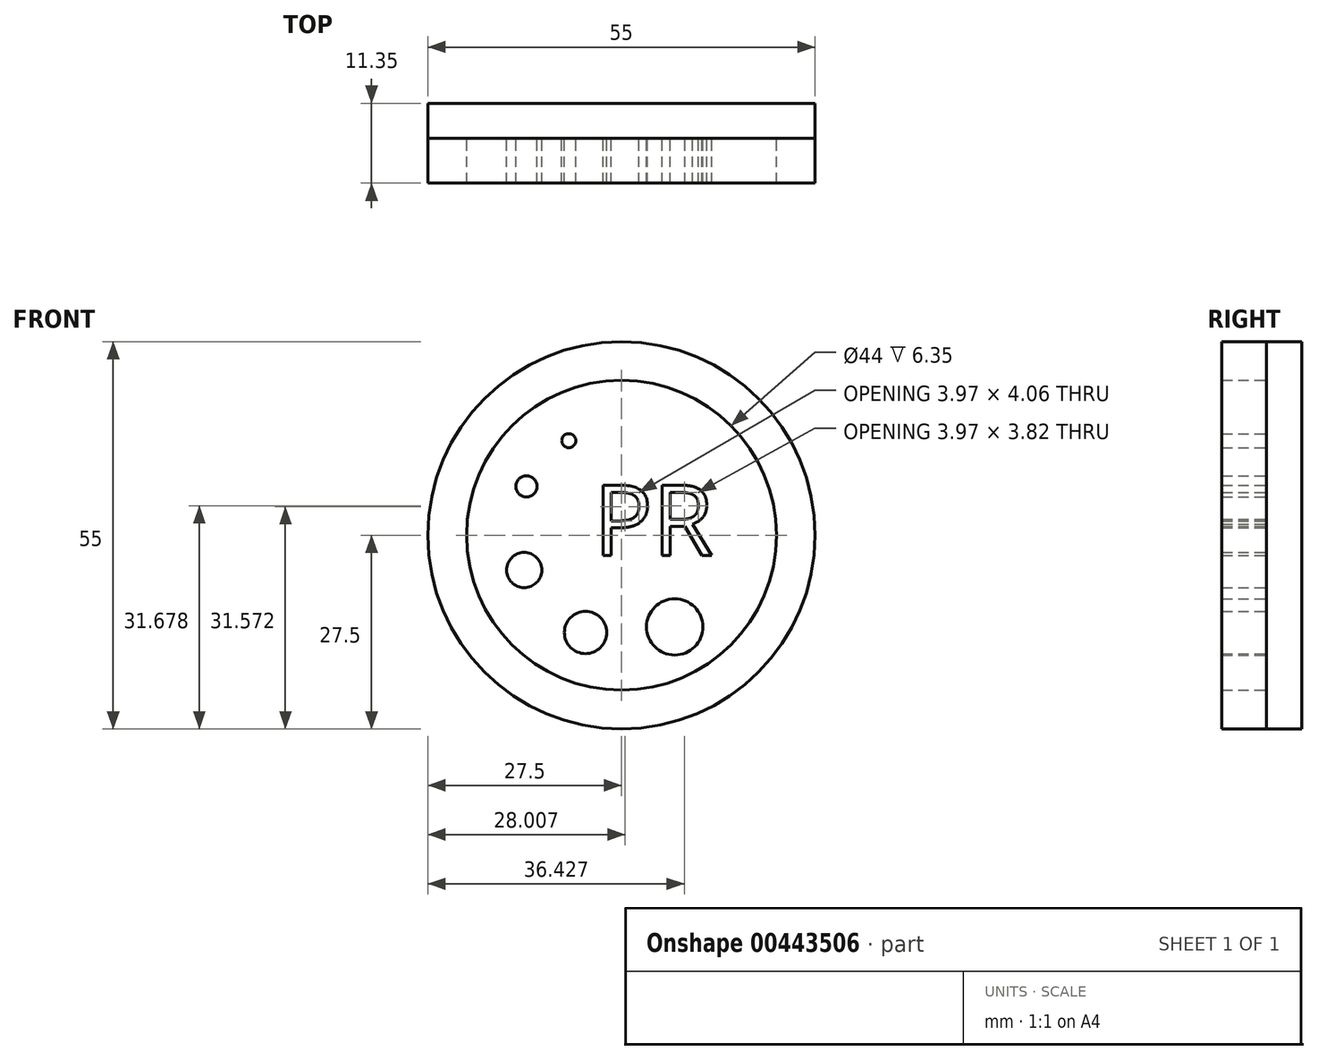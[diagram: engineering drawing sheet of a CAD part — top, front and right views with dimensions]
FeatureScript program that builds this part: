
annotation { "Feature Type Name" : "Feature", "Feature Type Description" : "" }
export const myFeature = defineFeature(function(context is Context, id is Id, definition is map)
    precondition{}
    {
        {
            var Q0;
            Q0=qCreatedBy(makeId("Front.planeOp"),FACE);
            var sketch = newSketch(context, id + "F0", { "sketchPlane" : qUnion([Q0])});
            skCircle(sketch, "E0", {"center": v(0, 0) * mm, "radius": 27.5 * mm});
            skCircle(sketch, "E1", {"center": v(0, 0) * mm, "radius": 22 * mm});
            skCircle(sketch, "E2", {"center": v(-7.49, 13.43) * mm, "radius": 1 * mm});
            skCircle(sketch, "E3", {"center": v(-13.5, 6.94) * mm, "radius": 1.5 * mm});
            skCircle(sketch, "E4", {"center": v(-13.82, -4.94) * mm, "radius": 2.5 * mm});
            skCircle(sketch, "E5", {"center": v(7.56, -13.02) * mm, "radius": 4 * mm});
            skCircle(sketch, "E6", {"center": v(-5.11, -13.8) * mm, "radius": 3 * mm});
            skText(sketch, "E7", { "text": "PR", "fontName": "OpenSans-Regular.ttf"});
            const initialGuessF0  = {"E7": [-0.00401, -0.00288, 1, 0, 0.01007]};
            skSetInitialGuess(sketch, initialGuessF0);
            skSolve(sketch);
        }
        {
            var Q0;
            Q0 = qSketchRegion(id + "F0", true);
            var Q1;
            Q1=makeQuery(id+"F0.imprint","IMPRINT",FACE,{"disambiguationData":[TD([[makeQuery(id+"F0.imprint","IMPRINT",EDGE,{"derivedFrom":sQuery(id+"F0.wireOp",EDGE,"E2")}),1.0]])]});
            var Q2;
            Q2=makeQuery(id+"F0.imprint","IMPRINT",FACE,{"disambiguationData":[TD([[makeQuery(id+"F0.imprint","IMPRINT",EDGE,{"derivedFrom":sQuery(id+"F0.wireOp",EDGE,"E3")}),1.0]])]});
            var Q3;
            Q3=makeQuery(id+"F0.imprint","IMPRINT",FACE,{"disambiguationData":[TD([[makeQuery(id+"F0.imprint","IMPRINT",EDGE,{"derivedFrom":sQuery(id+"F0.wireOp",EDGE,"E4")}),1.0]])]});
            var Q4;
            Q4=makeQuery(id+"F0.imprint","IMPRINT",FACE,{"disambiguationData":[TD([[makeQuery(id+"F0.imprint","IMPRINT",EDGE,{"derivedFrom":sQuery(id+"F0.wireOp",EDGE,"E6")}),1.0]])]});
            var Q5;
            Q5=makeQuery(id+"F0.imprint","IMPRINT",FACE,{"disambiguationData":[TD([[makeQuery(id+"F0.imprint","IMPRINT",EDGE,{"derivedFrom":sQuery(id+"F0.wireOp",EDGE,"E5")}),1.0]])]});
            var Q6;
            Q6=makeQuery(id+"F0.imprint","IMPRINT",FACE,{"disambiguationData":[TD([[makeQuery(id+"F0.imprint","IMPRINT",EDGE,{"derivedFrom":sQuery(id+"F0.wireOp",EDGE,"E7.sketch_text.stroke-0")}),-1.0]])]});
            var Q7;
            Q7=makeQuery(id+"F0.imprint","IMPRINT",FACE,{"disambiguationData":[TD([[makeQuery(id+"F0.imprint","IMPRINT",EDGE,{"derivedFrom":sQuery(id+"F0.wireOp",EDGE,"E7.sketch_text.stroke-15")}),-1.0]])]});
            extrude(context, id + "F1", {"entities" : qUnion([Q0, Q1, Q2, Q3, Q4, Q5, Q6, Q7]), "depth" : 6.35 * mm});
        }
        {
            var Q0;
            Q0=qCreatedBy(makeId("Front.planeOp"),FACE);
            var sketch = newSketch(context, id + "F2", { "sketchPlane" : qUnion([Q0])});
            skCircle(sketch, "E8", {"center": v(0, 0) * mm, "radius": 27.5 * mm});
            skSolve(sketch);
        }
        {
            var Q0;
            Q0 = qSketchRegion(id + "F2", true);
            extrude(context, id + "F3", {"entities" : qUnion([Q0]), "oppositeDirection" : true, "depth" : 5 * mm});
        }
    });
